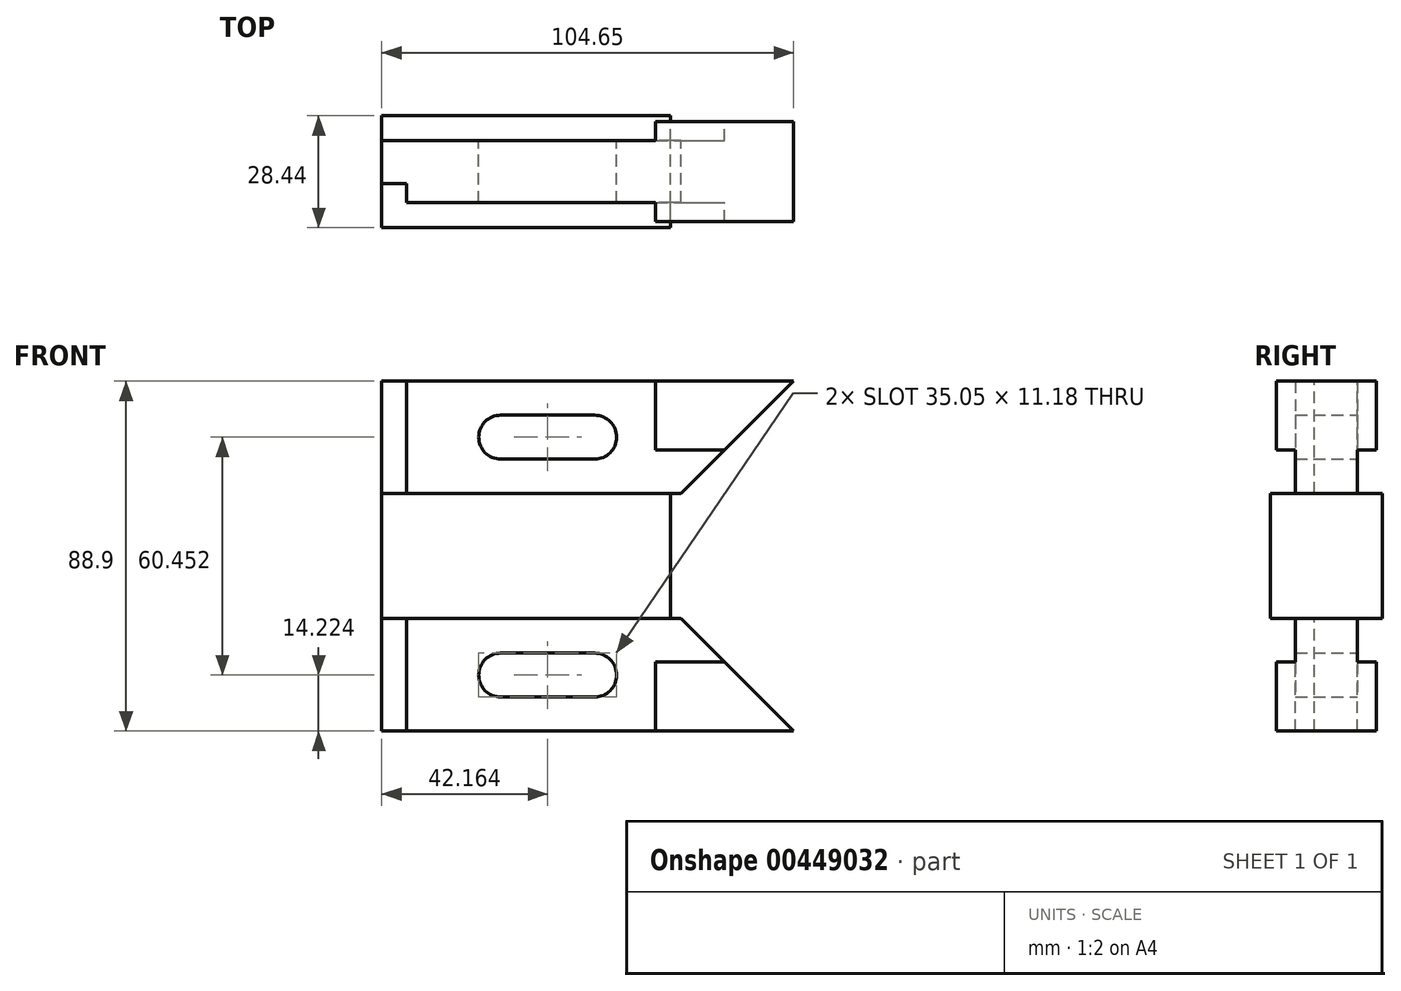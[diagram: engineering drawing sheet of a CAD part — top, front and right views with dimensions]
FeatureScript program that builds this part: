
annotation { "Feature Type Name" : "Feature", "Feature Type Description" : "" }
export const myFeature = defineFeature(function(context is Context, id is Id, definition is map)
    precondition{}
    {
        {
            var Q0;
            Q0=qCreatedBy(makeId("Front.planeOp"),FACE);
            var sketch = newSketch(context, id + "F0", { "sketchPlane" : qUnion([Q0])});
            skLineSegment(sketch, "E0", {"start": v(0, 0) * mm, "end": v(0, 88.9) * mm});
            skLineSegment(sketch, "E1", {"start": v(0, 0) * mm, "end": v(104.65, 0) * mm});
            skLineSegment(sketch, "E2", {"start": v(104.65, 0) * mm, "end": v(76.07, 28.58) * mm});
            skLineSegment(sketch, "E3", {"start": v(76.07, 28.58) * mm, "end": v(73.4, 28.58) * mm});
            skLineSegment(sketch, "E4", {"start": v(73.4, 28.58) * mm, "end": v(73.4, 60.33) * mm});
            skLineSegment(sketch, "E5", {"start": v(73.4, 60.33) * mm, "end": v(76.07, 60.33) * mm});
            skLineSegment(sketch, "E6", {"start": v(76.07, 60.32) * mm, "end": v(104.65, 88.9) * mm});
            skLineSegment(sketch, "E7", {"start": v(104.65, 88.9) * mm, "end": v(0, 88.9) * mm});
            skLineSegment(sketch, "E8", {"start": v(73.4, 60.33) * mm, "end": v(0, 60.33) * mm});
            skLineSegment(sketch, "E9", {"start": v(73.4, 28.58) * mm, "end": v(0, 28.58) * mm});
            skArc(sketch, "E10", {"start": v(30.23, 19.81) * mm, "mid": v(24.64, 14.22) * mm, "end": v(30.23, 8.64) * mm});
            skArc(sketch, "E11", {"start": v(54.1, 8.64) * mm, "mid": v(59.7, 14.22) * mm, "end": v(54.1, 19.81) * mm});
            skArc(sketch, "E12", {"start": v(30.23, 80.26) * mm, "mid": v(24.64, 74.68) * mm, "end": v(30.23, 69.09) * mm});
            skArc(sketch, "E13", {"start": v(54.1, 69.09) * mm, "mid": v(59.69, 74.68) * mm, "end": v(54.1, 80.26) * mm});
            skLineSegment(sketch, "E14", {"start": v(30.23, 19.81) * mm, "end": v(54.1, 19.81) * mm});
            skLineSegment(sketch, "E15", {"start": v(30.23, 8.64) * mm, "end": v(54.1, 8.64) * mm});
            skLineSegment(sketch, "E16", {"start": v(30.23, 80.26) * mm, "end": v(54.1, 80.26) * mm});
            skLineSegment(sketch, "E17", {"start": v(30.23, 69.09) * mm, "end": v(54.1, 69.09) * mm});
            skLineSegment(sketch, "E18", {"start": v(69.6, 88.9) * mm, "end": v(69.6, 71.37) * mm});
            skLineSegment(sketch, "E19", {"start": v(69.6, 71.37) * mm, "end": v(87.12, 71.37) * mm});
            skLineSegment(sketch, "E20", {"start": v(-26.76, 44.45) * mm, "end": v(121.46, 44.45) * mm, "construction": true});
            skLineSegment(sketch, "E21", {"start": v(69.6, 0) * mm, "end": v(69.6, 17.53) * mm});
            skLineSegment(sketch, "E22", {"start": v(69.6, 17.53) * mm, "end": v(87.12, 17.53) * mm});
            skLineSegment(sketch, "E23", {"start": v(6.35, 88.9) * mm, "end": v(6.35, 60.33) * mm});
            skLineSegment(sketch, "E24", {"start": v(6.35, 28.58) * mm, "end": v(6.35, 0) * mm});
            skSolve(sketch);
        }
        {
            var Q0;
            {var subQ4=sQuery(id+"F0.wireOp",EDGE,"E4");Q0=makeQuery(id+"F0.imprint","IMPRINT",FACE,{"disambiguationData":[TD([[makeQuery(id+"F0.imprint","IMPRINT",EDGE,{"derivedFrom":subQ4}),1.0]])]});}
            extrude(context, id + "F1", {"entities" : qUnion([Q0]), "endBound" : BoundingType.SYMMETRIC, "depth" : 28.45 * mm});
        }
        {
            var Q0;
            {var subQ2=sQuery(id+"F0.wireOp",EDGE,"E5");Q0=makeQuery(id+"F0.imprint","IMPRINT",FACE,{"disambiguationData":[TD([[makeQuery(id+"F0.imprint","IMPRINT",EDGE,{"derivedFrom":subQ2}),1.0]])]});}
            var Q1;
            {var subQ5=sQuery(id+"F0.wireOp",EDGE,"E23");Q1=makeQuery(id+"F0.imprint","IMPRINT",FACE,{"disambiguationData":[TD([[makeQuery(id+"F0.imprint","IMPRINT",EDGE,{"derivedFrom":subQ5}),-1.0]])]});}
            extrude(context, id + "F2", {"entities" : qUnion([Q0, Q1]), "operationType" : NewBodyOperationType.ADD, "endBound" : BoundingType.SYMMETRIC, "depth" : 15.75 * mm});
        }
        {
            var Q0;
            {var subQ1=sQuery(id+"F0.wireOp",EDGE,"E3");Q0=makeQuery(id+"F0.imprint","IMPRINT",FACE,{"disambiguationData":[TD([[makeQuery(id+"F0.imprint","IMPRINT",EDGE,{"derivedFrom":subQ1}),1.0]])]});}
            var Q1;
            {var subQ5=sQuery(id+"F0.wireOp",EDGE,"E24");Q1=makeQuery(id+"F0.imprint","IMPRINT",FACE,{"disambiguationData":[TD([[makeQuery(id+"F0.imprint","IMPRINT",EDGE,{"derivedFrom":subQ5}),-1.0]])]});}
            extrude(context, id + "F3", {"entities" : qUnion([Q0, Q1]), "operationType" : NewBodyOperationType.ADD, "endBound" : BoundingType.SYMMETRIC, "depth" : 15.75 * mm});
        }
        {
            var Q0;
            {var subQ4=sQuery(id+"F0.wireOp",EDGE,"E18");Q0=makeQuery(id+"F0.imprint","IMPRINT",FACE,{"disambiguationData":[TD([[makeQuery(id+"F0.imprint","IMPRINT",EDGE,{"derivedFrom":subQ4}),1.0]])]});}
            var Q1;
            {var subQ3=sQuery(id+"F0.wireOp",EDGE,"E21");Q1=makeQuery(id+"F0.imprint","IMPRINT",FACE,{"disambiguationData":[TD([[makeQuery(id+"F0.imprint","IMPRINT",EDGE,{"derivedFrom":subQ3}),-1.0]])]});}
            extrude(context, id + "F4", {"entities" : qUnion([Q0, Q1]), "operationType" : NewBodyOperationType.ADD, "endBound" : BoundingType.SYMMETRIC, "depth" : 25.4 * mm});
        }
        {
            var Q0;
            Q0=makeQuery(id+"F3.opExtrude","CAP_FACE",FACE,{"disambiguationData":[OSD([sQuery(id+"F0.wireOp",EDGE,"E0"),sQuery(id+"F0.wireOp",EDGE,"E1"),sQuery(id+"F0.wireOp",EDGE,"E2"),sQuery(id+"F0.wireOp",EDGE,"E3"),sQuery(id+"F0.wireOp",EDGE,"E9"),sQuery(id+"F0.wireOp",EDGE,"E10"),sQuery(id+"F0.wireOp",EDGE,"E11"),sQuery(id+"F0.wireOp",EDGE,"E14"),sQuery(id+"F0.wireOp",EDGE,"E15"),sQuery(id+"F0.wireOp",EDGE,"E21"),sQuery(id+"F0.wireOp",EDGE,"E22")])],"isStart":false});
            var sketch = newSketch(context, id + "F5", { "sketchPlane" : qUnion([Q0])});
            skLineSegment(sketch, "E25.bottom", {"start": v(0, 0) * mm, "end": v(6.35, 0) * mm});
            skLineSegment(sketch, "E25.top", {"start": v(0, 28.58) * mm, "end": v(6.35, 28.58) * mm});
            skLineSegment(sketch, "E25.left", {"start": v(0, 0) * mm, "end": v(0, 28.58) * mm});
            skLineSegment(sketch, "E25.right", {"start": v(6.35, 0) * mm, "end": v(6.35, 28.58) * mm});
            skSolve(sketch);
        }
        {
            var Q0;
            Q0=makeQuery(id+"F5.imprint","IMPRINT",FACE,{"disambiguationData":[TD([[makeQuery(id+"F5.imprint","IMPRINT",EDGE,{"derivedFrom":sQuery(id+"F5.wireOp",EDGE,"E25.bottom")}),1.0]])]});
            extrude(context, id + "F6", {"entities" : qUnion([Q0]), "operationType" : NewBodyOperationType.REMOVE, "oppositeDirection" : true, "depth" : 4.83 * mm});
        }
        {
            var Q0;
            Q0=makeQuery(id+"F2.opExtrude","CAP_FACE",FACE,{"disambiguationData":[OSD([sQuery(id+"F0.wireOp",EDGE,"E0"),sQuery(id+"F0.wireOp",EDGE,"E5"),sQuery(id+"F0.wireOp",EDGE,"E6"),sQuery(id+"F0.wireOp",EDGE,"E7"),sQuery(id+"F0.wireOp",EDGE,"E8"),sQuery(id+"F0.wireOp",EDGE,"E12"),sQuery(id+"F0.wireOp",EDGE,"E13"),sQuery(id+"F0.wireOp",EDGE,"E16"),sQuery(id+"F0.wireOp",EDGE,"E17"),sQuery(id+"F0.wireOp",EDGE,"E18"),sQuery(id+"F0.wireOp",EDGE,"E19")])],"isStart":false});
            var sketch = newSketch(context, id + "F7", { "sketchPlane" : qUnion([Q0])});
            skLineSegment(sketch, "E26.bottom", {"start": v(6.35, 88.9) * mm, "end": v(0, 88.9) * mm});
            skLineSegment(sketch, "E26.top", {"start": v(6.35, 60.33) * mm, "end": v(0, 60.33) * mm});
            skLineSegment(sketch, "E26.left", {"start": v(6.35, 88.9) * mm, "end": v(6.35, 60.33) * mm});
            skLineSegment(sketch, "E26.right", {"start": v(0, 88.9) * mm, "end": v(0, 60.33) * mm});
            skSolve(sketch);
        }
        {
            var Q0;
            Q0=makeQuery(id+"F7.imprint","IMPRINT",FACE,{"disambiguationData":[TD([[makeQuery(id+"F7.imprint","IMPRINT",EDGE,{"derivedFrom":sQuery(id+"F7.wireOp",EDGE,"E26.bottom")}),1.0]])]});
            extrude(context, id + "F8", {"entities" : qUnion([Q0]), "operationType" : NewBodyOperationType.REMOVE, "oppositeDirection" : true, "depth" : 4.83 * mm});
        }
    });
